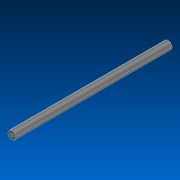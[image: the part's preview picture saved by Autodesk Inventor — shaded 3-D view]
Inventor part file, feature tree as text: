
AUTODESK INVENTOR PART (.ipt)
format: ipt  version: 2022.2 (Build 262287000, 287)  size: 121,344 bytes
history: native  units: in
note: dims shown in document units (in); Inventor stores cm internally (conversion verified against a paired STEP export)
features: extrude x1, sketch x1, other x1
ambient origin geometry x8: Origin, YZ Plane, XZ Plane, XY Plane, X Axis, Y Axis, Z Axis, Center Point
bodies: Solid1 (feature_tree)
feature tree (3):
  extrude  "Extrusion1"  TaperAngle=0.0deg  [1 undecoded]
  sketch  "Sketch1"  dims[d0=25.5in d1=0.0in]
  other  "Cut-Extrude2"
note: 1 required parameter value undecoded (feature->parameter linkage not recoverable at this tier; creation-order binding heuristic only, values carry confidence <= 0.55)
